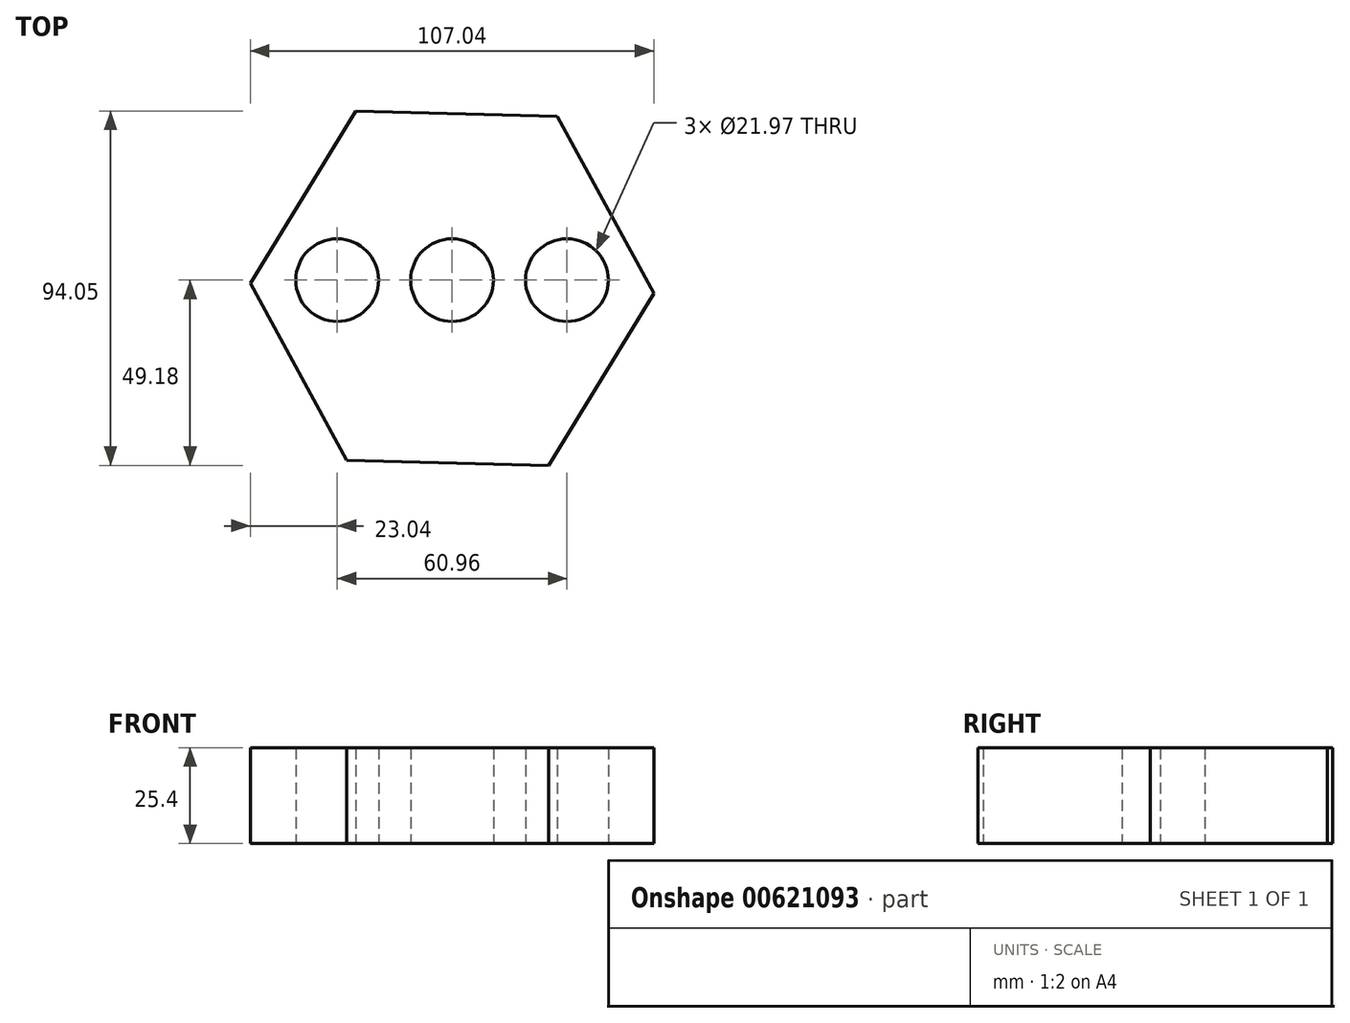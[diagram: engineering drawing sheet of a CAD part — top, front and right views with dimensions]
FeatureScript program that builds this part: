
annotation { "Feature Type Name" : "Feature", "Feature Type Description" : "" }
export const myFeature = defineFeature(function(context is Context, id is Id, definition is map)
    precondition{}
    {
        {
            var Q0;
            Q0=qCreatedBy(makeId("Top.planeOp"),FACE);
            var sketch = newSketch(context, id + "F0", { "sketchPlane" : qUnion([Q0])});
            skCircle(sketch, "E0", {"center": v(0, 0) * mm, "radius": 10.99 * mm});
            skCircle(sketch, "E1", {"center": v(-30.48, 0) * mm, "radius": 10.99 * mm});
            skCircle(sketch, "E2", {"center": v(30.48, 0) * mm, "radius": 10.99 * mm});
            skLineSegment(sketch, "E3", {"start": v(-30.48, 0) * mm, "end": v(0, 0) * mm});
            skLineSegment(sketch, "E4", {"start": v(0, 0) * mm, "end": v(30.48, 0) * mm});
            skCircle(sketch, "E5.cCircle", {"center": v(0, -2.16) * mm, "radius": 46.36 * mm, "construction": true});
            skLineSegment(sketch, "E5.0", {"start": v(27.93, 43.51) * mm, "end": v(53.52, -3.5) * mm});
            skLineSegment(sketch, "E5.1", {"start": v(53.52, -3.5) * mm, "end": v(25.59, -49.18) * mm});
            skLineSegment(sketch, "E5.2", {"start": v(25.59, -49.18) * mm, "end": v(-27.93, -47.83) * mm});
            skLineSegment(sketch, "E5.3", {"start": v(-27.93, -47.83) * mm, "end": v(-53.52, -0.8) * mm});
            skLineSegment(sketch, "E5.4", {"start": v(-53.52, -0.8) * mm, "end": v(-25.59, 44.87) * mm});
            skLineSegment(sketch, "E5.5", {"start": v(-25.59, 44.87) * mm, "end": v(27.93, 43.51) * mm});
            skPoint(sketch, "E5.0.midPoint", {"position": v(40.72, 20) * mm});
            skArc(sketch, "E6.cCircle", {"start": v(-53.32, -0.48) * mm, "mid": v(-53.33, -0.81) * mm, "end": v(-53.34, -1.14) * mm, "construction": true});
            skPoint(sketch, "E6.0.midPoint", {"position": v(46.86, 23.34) * mm});
            skPoint(sketch, "E7.0.midPoint", {"position": v(52.73, 28.7) * mm});
            skArc(sketch, "E8.trimOffspring", {"start": v(-25.2, 44.86) * mm, "mid": v(-25.5, 44.7) * mm, "end": v(-25.79, 44.54) * mm, "construction": true});
            skPoint(sketch, "E9.orphan", {"position": v(-29.44, 51.95) * mm});
            skPoint(sketch, "E10.orphan", {"position": v(-33.13, 60.89) * mm});
            skArc(sketch, "E11.trimOffspring", {"start": v(28.11, 43.18) * mm, "mid": v(27.83, 43.35) * mm, "end": v(27.55, 43.52) * mm, "construction": true});
            skPoint(sketch, "E6.0.start.orphan", {"position": v(32.14, 50.4) * mm});
            skArc(sketch, "E12.trimOffspring", {"start": v(25.2, -49.17) * mm, "mid": v(25.5, -49.02) * mm, "end": v(25.79, -48.86) * mm, "construction": true});
            skArc(sketch, "E13.trimOffspring", {"start": v(-28.11, -47.5) * mm, "mid": v(-27.83, -47.67) * mm, "end": v(-27.55, -47.84) * mm, "construction": true});
            skPoint(sketch, "E7.0.end.orphan", {"position": v(69.3, -1.75) * mm});
            skPoint(sketch, "E14.trimOffspring.end.orphan", {"position": v(61.58, -3.71) * mm});
            skPoint(sketch, "E7.5.end.orphan", {"position": v(36.16, 59.14) * mm});
            skSolve(sketch);
        }
        {
            var Q0;
            Q0=makeQuery(id+"F0.imprint","IMPRINT",FACE,{"disambiguationData":[TD([[makeQuery(id+"F0.imprint","IMPRINT",EDGE,{"derivedFrom":sQuery(id+"F0.wireOp",EDGE,"E1")}),-1.0]])]});
            var Q1;
            Q1=makeQuery(id+"F0.imprint","IMPRINT",FACE,{"disambiguationData":[TD([[makeQuery(id+"F0.imprint","IMPRINT",EDGE,{"derivedFrom":sQuery(id+"F0.wireOp",EDGE,"E6.0")}),1.0]])]});
            extrude(context, id + "F1", {"entities" : qUnion([Q0, Q1]), "depth" : 25.4 * mm, "offsetDistance" : 25.4 * mm});
        }
    });
